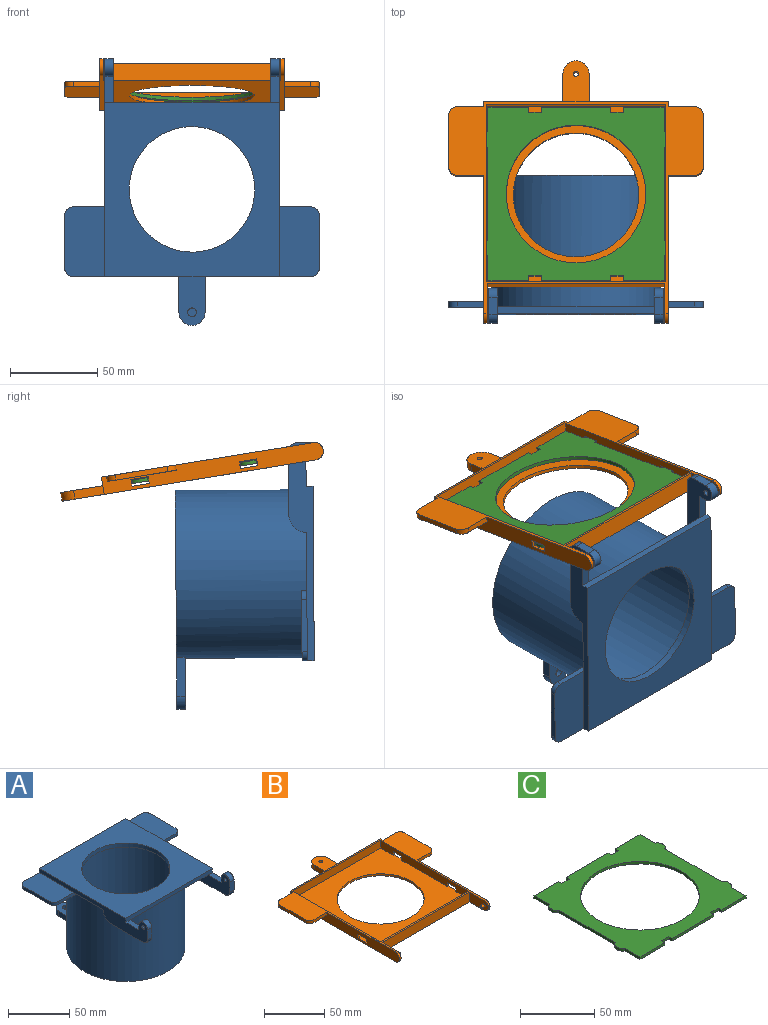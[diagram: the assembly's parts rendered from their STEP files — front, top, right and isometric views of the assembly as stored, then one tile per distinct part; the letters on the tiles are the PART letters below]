
ASSEMBLY  parts=3 mates=2
PART A: 52 faces, bbox 146x152.5x85 mm
  f0: plane 36.92x5mm, normal (0,0,-1), area 184.6mm2, adj f1,f36,f37,f40
  f1: plane 125x20mm, normal (1,0,0), area 969.8mm2, adj f0,f2,f14,f15,f18,f29,f35,f37
  f2: plane 100x60mm, normal (0,0,-1), area 1112.1mm2, adj f1,f3,f14,f17,f20,f27,f36,f37
  f3: cylinder r=48.3mm len=96.6mm, axis (0,0,-1), area 22523.2mm2, adj f2,f4,f6,f7,f8,f9,f19,f20
  f4: plane 69.65x16.43mm, normal (0,0,-1), area 335.5mm2, adj f3,f15,f19,f21,f28,f30
  f5: cylinder r=45.3mm len=90.6mm, axis (0,0,-1), area 21347.1mm2, adj f6,f13
  f6: plane 125.8x96.6mm, normal (0,0,-1), area 1298.9mm2, adj f3,f5,f8,f9,f10
  f7: plane 29.79x15mm, normal (0,0,1), area 397.1mm2, adj f3,f8,f9,f10,f11
  f8: plane 22.29x5mm, normal (-1,0,0), area 111.4mm2, adj f3,f6,f7,f10
  f9: plane 22.29x5mm, normal (1,0,0), area 111.4mm2, adj f3,f6,f7,f10
  f10: cylinder r=7.5mm len=15mm, axis (0,0,-1), area 117.8mm2, adj f6,f7,f8,f9
  f11: cylinder r=2.5mm len=5mm, axis (0,0,1), area 47.1mm2, adj f7,f12
  f12: plane 5x5mm, normal (0,0,1), area 19.6mm2, adj f11
  f13: plane 90.6x90.6mm, normal (0,0,-1), area 2375.3mm2, adj f5,f16
  f14: plane 100x4mm, normal (0,-1,0), area 400mm2, adj f1,f2,f17,f18,f35,f47
  f15: plane 136x7mm, normal (0,1,0), area 599.1mm2, adj f1,f4,f17,f18,f21,f24,f25,f26
  f16: cylinder r=36mm len=72mm, axis (0,0,-1), area 904.8mm2, adj f13,f18
  f17: plane 125x20mm, normal (-1,0,0), area 969.8mm2, adj f2,f14,f15,f18,f26,f43,f44,f45
  f18: plane 100x100mm, normal (0,0,1), area 5928.5mm2, adj f1,f14,f15,f16,f17
  f19: plane 9.28x4.41mm, normal (0.9,-0.43,0), area 30.8mm2, adj f3,f4,f21,f25
  f20: plane 20.75x3mm, normal (0,-1,0), area 62.2mm2, adj f2,f3,f22,f25,f26
  f21: cylinder r=5mm len=7.15mm, axis (0,0,1), area 30.2mm2, adj f4,f15,f19,f25
  f22: cylinder r=5mm len=5mm, axis (0,0,1), area 23.6mm2, adj f20,f23,f25,f26
  f23: plane 30x3mm, normal (-1,0,0), area 90mm2, adj f22,f24,f25,f26
  f24: cylinder r=5mm len=5mm, axis (0,0,1), area 23.6mm2, adj f15,f23,f25,f26
  f25: plane 43.18x40mm, normal (0,0,-1), area 1388.8mm2, adj f3,f15,f19,f20,f21,f22,f23,f24
  f26: plane 40x23mm, normal (0,0,1), area 909.3mm2, adj f15,f17,f20,f22,f23,f24
  f27: plane 20.75x3mm, normal (0,-1,0), area 62.2mm2, adj f2,f3,f29,f33,f34
  f28: plane 9.28x4.41mm, normal (-0.9,-0.43,0), area 30.8mm2, adj f3,f4,f30,f34
  f29: plane 40x23mm, normal (0,0,1), area 909.3mm2, adj f1,f15,f27,f31,f32,f33
  f30: cylinder r=5mm len=7.15mm, axis (0,0,1), area 30.2mm2, adj f4,f15,f28,f34
  f31: cylinder r=5mm len=5mm, axis (0,0,1), area 23.6mm2, adj f15,f29,f32,f34
  f32: plane 30x3mm, normal (1,0,0), area 90mm2, adj f29,f31,f33,f34
  f33: cylinder r=5mm len=5mm, axis (0,0,1), area 23.6mm2, adj f27,f29,f32,f34
  f34: plane 43.18x40mm, normal (0,0,-1), area 1388.8mm2, adj f3,f15,f27,f28,f30,f31,f32,f33
  f35: plane 15x5mm, normal (0,0,1), area 75mm2, adj f1,f14,f36,f38
  f36: plane 51.44x20mm, normal (-1,0,0), area 569.8mm2, adj f0,f2,f35,f37,f38,f39,f40,f41
  f37: cylinder r=10.01mm len=10mm, axis (1,0,0), area 76.2mm2, adj f0,f1,f2,f36
  f38: plane 5x5mm, normal (0,1,0), area 25mm2, adj f1,f35,f36,f41
  f39: plane 10x5mm, normal (0,-1,0), area 50mm2, adj f1,f36,f40,f41
  f40: cylinder r=5mm len=5mm, axis (1,0,0), area 39.3mm2, adj f0,f1,f36,f39
  f41: cylinder r=5mm len=10mm, axis (1,0,0), area 78.5mm2, adj f1,f36,f38,f39
  f42: cylinder r=1.5mm len=5mm, axis (1,0,0), area 47.1mm2, adj f1,f36
  f43: cylinder r=5mm len=5mm, axis (-1,0,0), area 39.3mm2, adj f17,f44,f50,f51
  f44: plane 10x5mm, normal (0,-1,0), area 50mm2, adj f17,f43,f45,f51
  f45: cylinder r=5mm len=10mm, axis (-1,0,0), area 78.5mm2, adj f17,f44,f46,f51
  f46: plane 5x5mm, normal (0,1,0), area 25mm2, adj f17,f45,f47,f51
  f47: plane 15x5mm, normal (0,0,1), area 75mm2, adj f14,f17,f46,f51
  f48: cylinder r=10.01mm len=10mm, axis (-1,0,0), area 76.2mm2, adj f2,f17,f50,f51
  f49: cylinder r=1.5mm len=5mm, axis (-1,0,0), area 47.1mm2, adj f17,f51
  f50: plane 36.92x5mm, normal (0,0,-1), area 184.6mm2, adj f17,f43,f48,f51
  f51: plane 51.44x20mm, normal (1,0,0), area 569.8mm2, adj f2,f43,f44,f45,f46,f47,f48,f49
PART B: 49 faces, bbox 146x152.5x10 mm
  f0: plane 128x10mm, normal (-1,0,0), area 1069.3mm2, adj f5,f8,f9,f11,f17,f18,f19,f20
  f1: plane 102x10mm, normal (0,-1,0), area 1020mm2, adj f8,f9,f29,f30
  f2: plane 103x8mm, normal (-1,0,0), area 744mm2, adj f3,f7,f8,f11,f23,f24,f25,f26
  f3: plane 103x8mm, normal (0,1,0), area 824mm2, adj f2,f4,f8,f11
  f4: plane 103x8mm, normal (1,0,0), area 744mm2, adj f3,f7,f8,f11,f17,f18,f19,f20
  f5: plane 106x10mm, normal (0,1,0), area 985mm2, adj f0,f6,f8,f9,f12,f14,f16
  f6: plane 128x10mm, normal (1,0,0), area 1069.3mm2, adj f5,f8,f9,f11,f23,f24,f25,f26
  f7: plane 103x8mm, normal (0,-1,0), area 824mm2, adj f2,f4,f8,f11
  f8: plane 146x123mm, normal (0,0,1), area 2273.5mm2, adj f0,f1,f2,f3,f4,f5,f6,f7
  f9: plane 147.5x106mm, normal (0,0,-1), area 7568.8mm2, adj f0,f1,f5,f6,f10,f12,f13,f14
  f10: cylinder r=36mm len=72mm, axis (0,0,-1), area 452.4mm2, adj f9,f11
  f11: plane 106x103mm, normal (0,0,1), area 6597.5mm2, adj f0,f2,f3,f4,f6,f7,f10,f17
  f12: plane 17x5mm, normal (1,0,0), area 85mm2, adj f5,f9,f13,f16
  f13: cylinder r=7.5mm len=15mm, axis (0,0,-1), area 117.8mm2, adj f9,f12,f14,f16
  f14: plane 17x5mm, normal (-1,0,0), area 85mm2, adj f5,f9,f13,f16
  f15: cylinder r=1.5mm len=5mm, axis (0,0,-1), area 47.1mm2, adj f9,f16
  f16: plane 24.5x15mm, normal (0,0,1), area 336.3mm2, adj f5,f12,f13,f14,f15
  f17: plane 4x1.5mm, normal (0,-1,0), area 6mm2, adj f0,f4,f11,f18
  f18: plane 10x1.5mm, normal (0,0,-1), area 15mm2, adj f0,f4,f17,f19
  f19: plane 4x1.5mm, normal (0,1,0), area 6mm2, adj f0,f4,f11,f18
  f20: plane 4x1.5mm, normal (0,-1,0), area 6mm2, adj f0,f4,f11,f21
  f21: plane 10x1.5mm, normal (0,0,-1), area 15mm2, adj f0,f4,f20,f22
  f22: plane 4x1.5mm, normal (0,1,0), area 6mm2, adj f0,f4,f11,f21
  f23: plane 4x1.5mm, normal (0,1,0), area 6mm2, adj f2,f6,f11,f24
  f24: plane 10x1.5mm, normal (0,0,-1), area 15mm2, adj f2,f6,f23,f25
  f25: plane 4x1.5mm, normal (0,-1,0), area 6mm2, adj f2,f6,f11,f24
  f26: plane 4x1.5mm, normal (0,1,0), area 6mm2, adj f2,f6,f11,f27
  f27: plane 10x1.5mm, normal (0,0,-1), area 15mm2, adj f2,f6,f26,f28
  f28: plane 4x1.5mm, normal (0,-1,0), area 6mm2, adj f2,f6,f11,f27
  f29: plane 22x10mm, normal (1,0,0), area 204.4mm2, adj f1,f8,f9,f31,f33
  f30: plane 22x10mm, normal (-1,0,0), area 204.4mm2, adj f1,f8,f9,f32,f35
  f31: cylinder r=5mm len=10mm, axis (-1,0,0), area 31.4mm2, adj f0,f8,f9,f29
  f32: cylinder r=5mm len=10mm, axis (1,0,0), area 31.4mm2, adj f6,f8,f9,f30
  f33: cylinder r=1.25mm len=3.5mm, axis (-1,0,0), area 27.5mm2, adj f29,f34
  f34: plane 2.5x2.5mm, normal (1,0,0), area 4.9mm2, adj f33
  f35: cylinder r=1.25mm len=3.5mm, axis (1,0,0), area 27.5mm2, adj f30,f36
  f36: plane 2.5x2.5mm, normal (-1,0,0), area 4.9mm2, adj f35
  f37: plane 15x3mm, normal (0,-1,0), area 45mm2, adj f6,f8,f38,f42
  f38: cylinder r=5mm len=5mm, axis (0,0,1), area 23.6mm2, adj f8,f37,f39,f42
  f39: plane 30x3mm, normal (1,0,0), area 90mm2, adj f8,f38,f40,f42
  f40: cylinder r=5mm len=5mm, axis (0,0,1), area 23.6mm2, adj f8,f39,f41,f42
  f41: plane 15x3mm, normal (0,1,0), area 45mm2, adj f6,f8,f40,f42
  f42: plane 40x20mm, normal (0,0,-1), area 789.3mm2, adj f6,f37,f38,f39,f40,f41
  f43: plane 15x3mm, normal (0,-1,0), area 45mm2, adj f0,f8,f44,f48
  f44: cylinder r=5mm len=5mm, axis (0,0,1), area 23.6mm2, adj f8,f43,f45,f48
  f45: plane 30x3mm, normal (-1,0,0), area 90mm2, adj f8,f44,f46,f48
  f46: cylinder r=5mm len=5mm, axis (0,0,1), area 23.6mm2, adj f8,f45,f47,f48
  f47: plane 15x3mm, normal (0,1,0), area 45mm2, adj f0,f8,f46,f48
  f48: plane 40x20mm, normal (0,0,-1), area 789.3mm2, adj f0,f43,f44,f45,f46,f47
PART C: 39 faces, bbox 106.6x101x2 mm
  f0: plane 14.5x2mm, normal (-1,0,0), area 29mm2, adj f1,f36,f37,f38
  f1: plane 2x0.8mm, normal (0,1,0), area 1.6mm2, adj f0,f2,f37,f38
  f2: cylinder r=6.06mm len=9mm, axis (0,0,-1), area 20.3mm2, adj f1,f3,f37,f38
  f3: plane 2x0.8mm, normal (0,-1,0), area 1.6mm2, adj f2,f4,f37,f38
  f4: plane 54x2mm, normal (-1,0,0), area 108mm2, adj f3,f5,f37,f38
  f5: plane 2x0.8mm, normal (0,1,0), area 1.6mm2, adj f4,f6,f37,f38
  f6: cylinder r=6.06mm len=9mm, axis (0,0,-1), area 20.3mm2, adj f5,f7,f37,f38
  f7: plane 2x0.8mm, normal (0,-1,0), area 1.6mm2, adj f6,f8,f37,f38
  f8: plane 14.5x2mm, normal (-1,0,0), area 29mm2, adj f7,f9,f37,f38
  f9: plane 23.5x2mm, normal (0,-1,0), area 47mm2, adj f8,f10,f37,f38
  f10: plane 3x2mm, normal (1,0,0), area 6mm2, adj f9,f11,f37,f38
  f11: plane 7x2mm, normal (0,-1,0), area 14mm2, adj f10,f12,f37,f38
  f12: plane 3x2mm, normal (-1,0,0), area 6mm2, adj f11,f13,f37,f38
  f13: plane 40x2mm, normal (0,-1,0), area 80mm2, adj f12,f14,f37,f38
  f14: plane 3x2mm, normal (1,0,0), area 6mm2, adj f13,f15,f37,f38
  f15: plane 7x2mm, normal (0,-1,0), area 14mm2, adj f14,f16,f37,f38
  f16: plane 3x2mm, normal (-1,0,0), area 6mm2, adj f15,f17,f37,f38
  f17: plane 23.5x2mm, normal (0,-1,0), area 47mm2, adj f16,f18,f37,f38
  f18: plane 14.5x2mm, normal (1,0,0), area 29mm2, adj f17,f19,f37,f38
  f19: plane 2x0.8mm, normal (0,-1,0), area 1.6mm2, adj f18,f20,f37,f38
  f20: cylinder r=6.06mm len=9mm, axis (0,0,-1), area 20.3mm2, adj f19,f21,f37,f38
  f21: plane 2x0.8mm, normal (0,1,0), area 1.6mm2, adj f20,f22,f37,f38
  f22: plane 54x2mm, normal (1,0,0), area 108mm2, adj f21,f23,f37,f38
  f23: plane 2x0.8mm, normal (0,-1,0), area 1.6mm2, adj f22,f24,f37,f38
  f24: cylinder r=6.06mm len=9mm, axis (0,0,-1), area 20.3mm2, adj f23,f25,f37,f38
  f25: plane 2x0.8mm, normal (0,1,0), area 1.6mm2, adj f24,f26,f37,f38
  f26: plane 14.5x2mm, normal (1,0,0), area 29mm2, adj f25,f27,f37,f38
  f27: plane 23.5x2mm, normal (0,1,0), area 47mm2, adj f26,f28,f37,f38
  f28: plane 3x2mm, normal (-1,0,0), area 6mm2, adj f27,f29,f37,f38
  f29: plane 7x2mm, normal (0,1,0), area 14mm2, adj f28,f30,f37,f38
  f30: plane 3x2mm, normal (1,0,0), area 6mm2, adj f29,f31,f37,f38
  f31: plane 40x2mm, normal (0,1,0), area 80mm2, adj f30,f32,f37,f38
  f32: plane 3x2mm, normal (-1,0,0), area 6mm2, adj f31,f33,f37,f38
  f33: plane 7x2mm, normal (0,1,0), area 14mm2, adj f32,f34,f37,f38
  f34: plane 3x2mm, normal (1,0,0), area 6mm2, adj f33,f36,f37,f38
  f35: cylinder r=40mm len=80mm, axis (0,0,-1), area 502.7mm2, adj f37,f38
  f36: plane 23.5x2mm, normal (0,1,0), area 47mm2, adj f0,f34,f37,f38
  f37: plane 106.6x101mm, normal (0,0,1), area 5169.1mm2, adj f0,f1,f2,f3,f4,f5,f6,f7
  f38: plane 106.6x101mm, normal (0,0,-1), area 5169.1mm2, adj f0,f1,f2,f3,f4,f5,f6,f7
PLACE A rot(axis=(0,-0.7,0.71),180deg) t=(0.88,40.98,-0.25)mm fixed
PLACE B rot(axis=(-1,0,0),9.2deg) t=(0.88,29.74,54.11)mm
PLACE C rot(axis=(-1,0,0),9.2deg) t=(0.88,30.31,57.56)mm
MATE revolute A.f41 <-> B.f31  axis (-1,0,0) through (-49.12,-38.54,70.29)mm
MATE fastened B.f10 <-> C.f35  axis (0,0.16,0.99) through (0.88,30.06,56.08)mm
